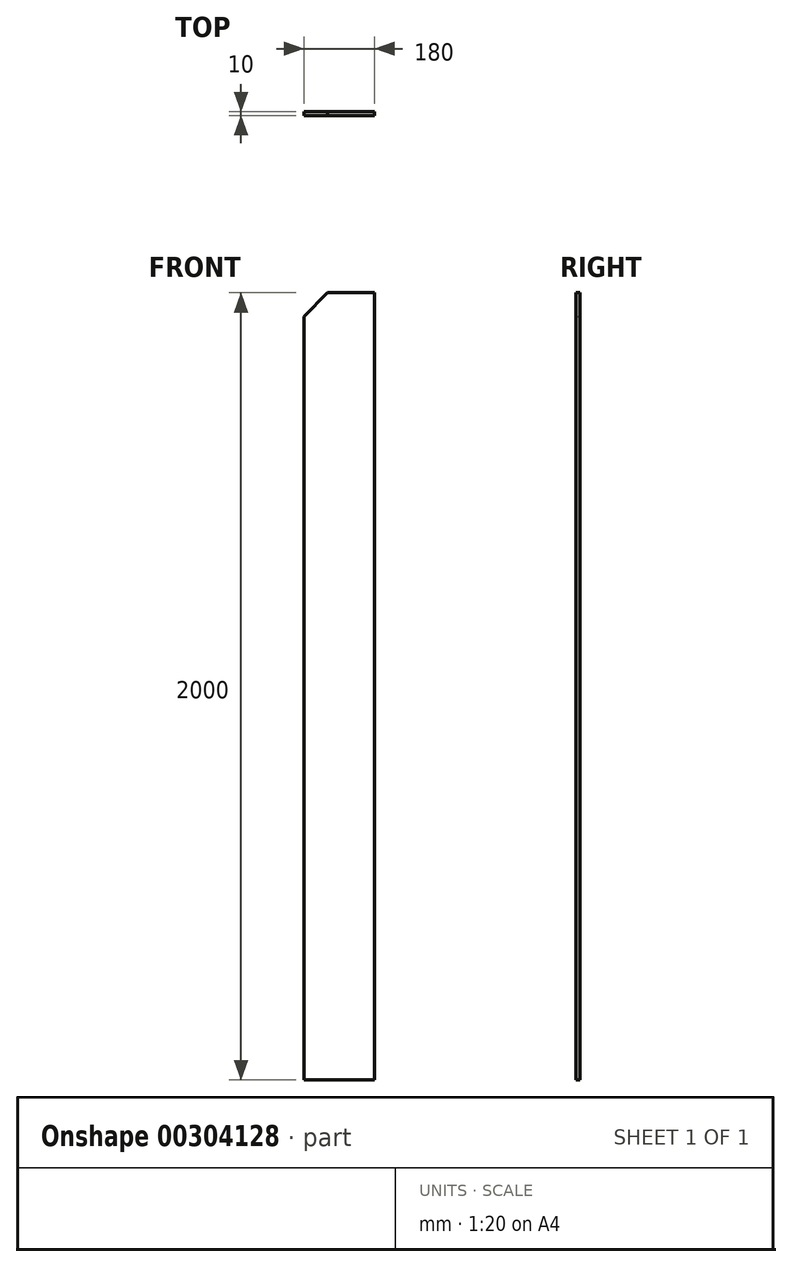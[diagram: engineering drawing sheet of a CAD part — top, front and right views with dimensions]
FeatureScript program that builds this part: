
annotation { "Feature Type Name" : "Feature", "Feature Type Description" : "" }
export const myFeature = defineFeature(function(context is Context, id is Id, definition is map)
    precondition{}
    {
        {
            var Q0;
            Q0=qCreatedBy(makeId("Top.planeOp"),FACE);
            var sketch = newSketch(context, id + "F0", { "sketchPlane" : qUnion([Q0])});
            skLineSegment(sketch, "E0.bottom", {"start": v(-58.4, 8.8) * mm, "end": v(121.6, 8.8) * mm});
            skLineSegment(sketch, "E0.top", {"start": v(-58.4, 18.8) * mm, "end": v(121.6, 18.8) * mm});
            skLineSegment(sketch, "E0.left", {"start": v(-58.4, 8.8) * mm, "end": v(-58.4, 18.8) * mm});
            skLineSegment(sketch, "E0.right", {"start": v(121.6, 8.8) * mm, "end": v(121.6, 18.8) * mm});
            skSolve(sketch);
        }
        {
            var Q0;
            Q0=makeQuery(id+"F0.imprint","IMPRINT",FACE,{"disambiguationData":[TD([[makeQuery(id+"F0.imprint","IMPRINT",EDGE,{"derivedFrom":sQuery(id+"F0.wireOp",EDGE,"E0.bottom")}),1.0]])]});
            extrude(context, id + "F1", {"entities" : qUnion([Q0]), "depth" : 2000 * mm, "offsetDistance" : 25 * mm});
        }
        {
            var Q0;
            Q0=makeQuery(id+"F1.opExtrude","CAP_EDGE",EDGE,{"disambiguationData":[OSD([sQuery(id+"F0.wireOp",EDGE,"E0.left")])],"isStart":false});
            chamfer(context, id + "F2", {"entities" : qUnion([Q0]), "width" : 60 * mm, "tangentPropagation" : true});
        }
    });
